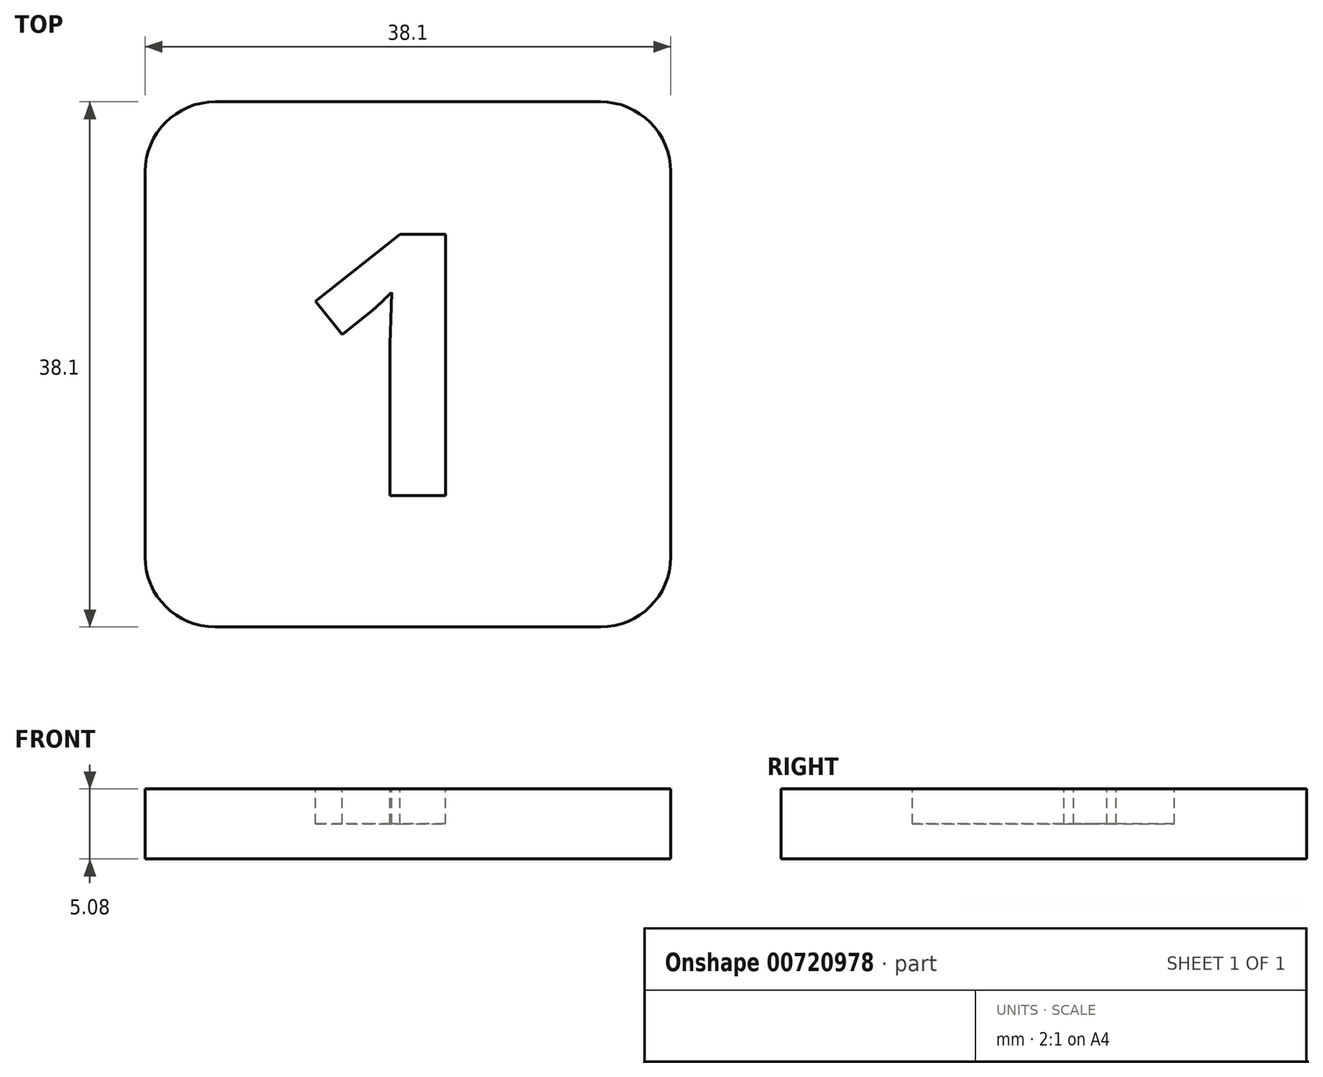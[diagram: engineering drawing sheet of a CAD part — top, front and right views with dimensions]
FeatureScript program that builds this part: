
annotation { "Feature Type Name" : "Feature", "Feature Type Description" : "" }
export const myFeature = defineFeature(function(context is Context, id is Id, definition is map)
    precondition{}
    {
        {
            var Q0;
            Q0=qCreatedBy(makeId("Top.planeOp"),FACE);
            var sketch = newSketch(context, id + "F0", { "sketchPlane" : qUnion([Q0])});
            skLineSegment(sketch, "E0.bottom", {"start": v(-19.05, 19.05) * mm, "end": v(19.05, 19.05) * mm});
            skLineSegment(sketch, "E0.top", {"start": v(-19.05, -19.05) * mm, "end": v(19.05, -19.05) * mm});
            skLineSegment(sketch, "E0.left", {"start": v(-19.05, 19.05) * mm, "end": v(-19.05, -19.05) * mm});
            skLineSegment(sketch, "E0.right", {"start": v(19.05, 19.05) * mm, "end": v(19.05, -19.05) * mm});
            skPoint(sketch, "E0.middle", {"position": v(0, 0) * mm});
            skSolve(sketch);
        }
        {
            var Q0;
            Q0 = qSketchRegion(id + "F0", true);
            extrude(context, id + "F1", {"entities" : qUnion([Q0]), "depth" : 5.08 * mm, "offsetDistance" : 25.4 * mm});
        }
        {
            var Q0;
            Q0=makeQuery(id+"F1.opExtrude","CAP_FACE",FACE,{"disambiguationData":[OSD([sQuery(id+"F0.wireOp",EDGE,"E0.bottom"),sQuery(id+"F0.wireOp",EDGE,"E0.top"),sQuery(id+"F0.wireOp",EDGE,"E0.left"),sQuery(id+"F0.wireOp",EDGE,"E0.right")])],"isStart":false});
            var sketch = newSketch(context, id + "F2", { "sketchPlane" : qUnion([Q0])});
            skText(sketch, "E1", { "text": "1", "fontName": "OpenSans-Bold.ttf"});
            const initialGuessF2  = {"E1": [-0.00826, -0.00952, 1, 0, 0.01913]};
            skSetInitialGuess(sketch, initialGuessF2);
            skSolve(sketch);
        }
        {
            var Q0;
            Q0 = qSketchRegion(id + "F2", true);
            extrude(context, id + "F3", {"entities" : qUnion([Q0]), "operationType" : NewBodyOperationType.REMOVE, "oppositeDirection" : true, "depth" : 2.54 * mm, "offsetDistance" : 25.4 * mm});
        }
        {
            var Q0;
            Q0=makeQuery(id+"F1.opExtrude","SWEPT_EDGE",EDGE,{"disambiguationData":[OSD([sQuery(id+"F0.wireOp",EDGE,"E0.top"),sQuery(id+"F0.wireOp",EDGE,"E0.left")])]});
            var Q1;
            Q1=makeQuery(id+"F1.opExtrude","SWEPT_EDGE",EDGE,{"disambiguationData":[OSD([sQuery(id+"F0.wireOp",EDGE,"E0.top"),sQuery(id+"F0.wireOp",EDGE,"E0.right")])]});
            var Q2;
            Q2=makeQuery(id+"F1.opExtrude","SWEPT_EDGE",EDGE,{"disambiguationData":[OSD([sQuery(id+"F0.wireOp",EDGE,"E0.bottom"),sQuery(id+"F0.wireOp",EDGE,"E0.right")])]});
            var Q3;
            Q3=makeQuery(id+"F1.opExtrude","SWEPT_EDGE",EDGE,{"disambiguationData":[OSD([sQuery(id+"F0.wireOp",EDGE,"E0.bottom"),sQuery(id+"F0.wireOp",EDGE,"E0.left")])]});
            fillet(context, id + "F4", {"entities" : qUnion([Q0, Q1, Q2, Q3]), "radius" : 5.08 * mm, "tangentPropagation" : true, "allowEdgeOverflow" : false});
        }
    });
